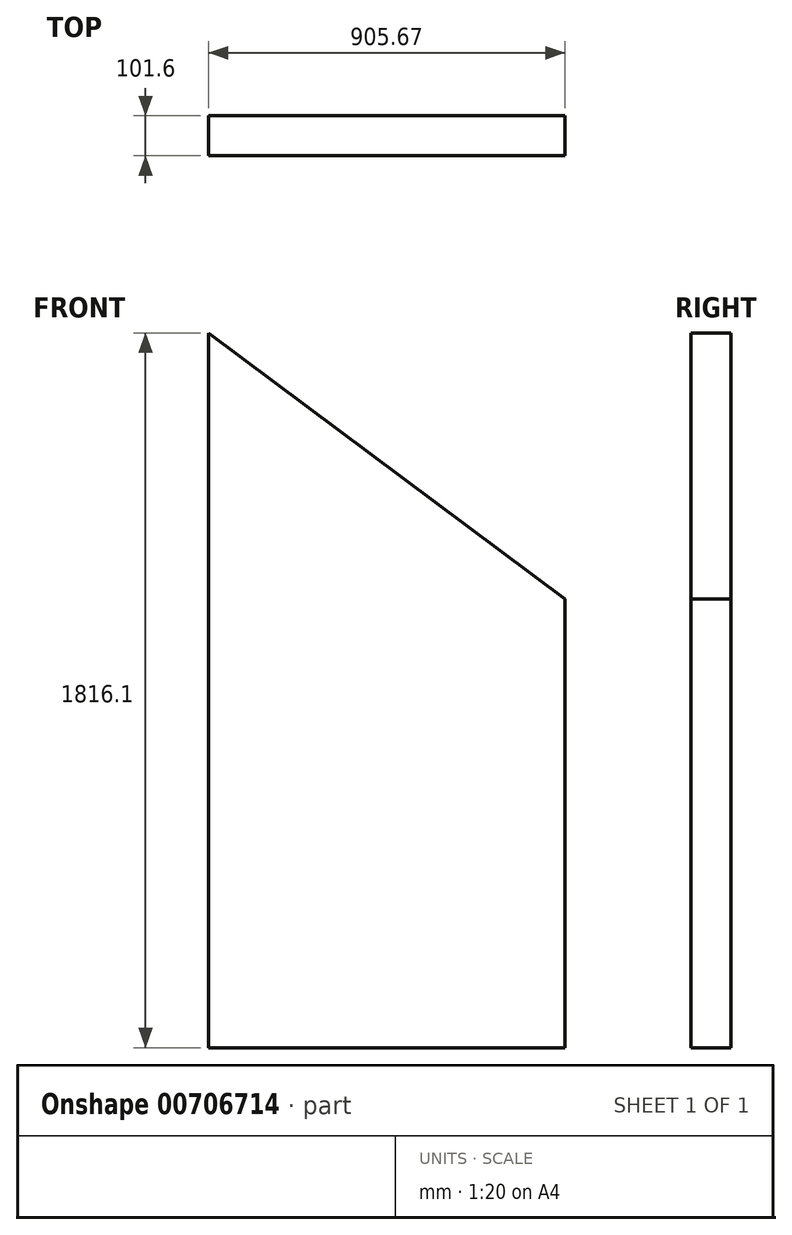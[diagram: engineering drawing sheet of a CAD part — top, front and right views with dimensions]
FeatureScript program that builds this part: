
annotation { "Feature Type Name" : "Feature", "Feature Type Description" : "" }
export const myFeature = defineFeature(function(context is Context, id is Id, definition is map)
    precondition{}
    {
        {
            var Q0;
            Q0=qCreatedBy(makeId("Front.planeOp"),FACE);
            var sketch = newSketch(context, id + "F0", { "sketchPlane" : qUnion([Q0])});
            skLineSegment(sketch, "E0", {"start": v(0, 0) * mm, "end": v(0, 1816.1) * mm});
            skLineSegment(sketch, "E1", {"start": v(0, 1816.1) * mm, "end": v(905.67, 1139.82) * mm});
            skLineSegment(sketch, "E2", {"start": v(905.67, 1139.83) * mm, "end": v(905.67, 0) * mm});
            skLineSegment(sketch, "E3", {"start": v(905.67, 0) * mm, "end": v(0, 0) * mm});
            skSolve(sketch);
        }
        {
            var Q0;
            Q0=makeQuery(id+"F0.imprint","IMPRINT",FACE,{"disambiguationData":[TD([[makeQuery(id+"F0.imprint","IMPRINT",EDGE,{"derivedFrom":sQuery(id+"F0.wireOp",EDGE,"E0")}),-1.0]])]});
            extrude(context, id + "F1", {"entities" : qUnion([Q0]), "depth" : 101.6 * mm, "offsetDistance" : 25.4 * mm});
        }
    });
